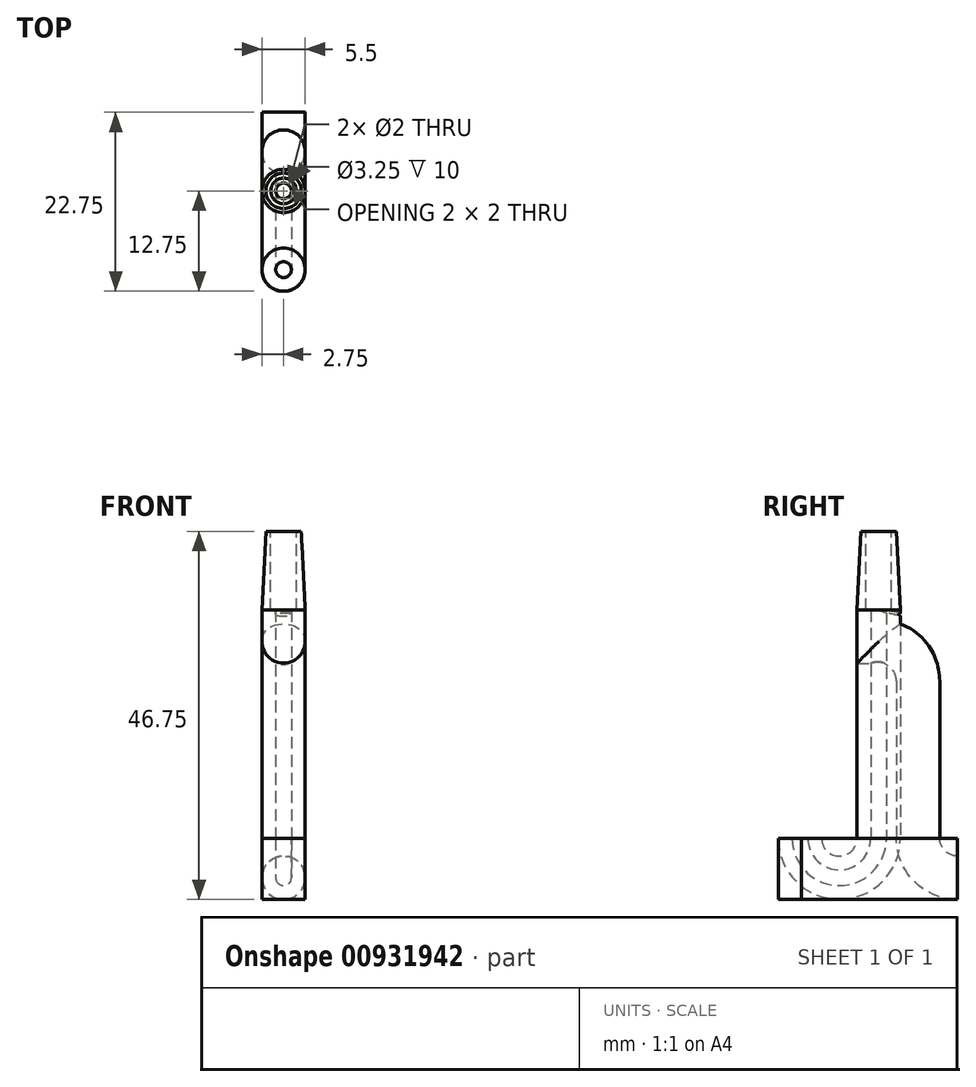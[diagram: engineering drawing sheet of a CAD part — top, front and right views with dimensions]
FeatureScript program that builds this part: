
annotation { "Feature Type Name" : "Feature", "Feature Type Description" : "" }
export const myFeature = defineFeature(function(context is Context, id is Id, definition is map)
    precondition{}
    {
        {
            var Q0;
            Q0=qCreatedBy(makeId("Front.planeOp"),FACE);
            var sketch = newSketch(context, id + "F0", { "sketchPlane" : qUnion([Q0])});
            skLineSegment(sketch, "E0", {"start": v(0, 0) * mm, "end": v(2.75, 0) * mm});
            skLineSegment(sketch, "E1", {"start": v(2.75, 0) * mm, "end": v(2.25, 10) * mm});
            skLineSegment(sketch, "E2", {"start": v(2.25, 10) * mm, "end": v(0, 10) * mm});
            skLineSegment(sketch, "E3", {"start": v(0, 10) * mm, "end": v(0, 0) * mm});
            skSolve(sketch);
        }
        {
            var Q0;
            Q0=makeQuery(id+"F0.imprint","IMPRINT",FACE,{"disambiguationData":[TD([[makeQuery(id+"F0.imprint","IMPRINT",EDGE,{"derivedFrom":sQuery(id+"F0.wireOp",EDGE,"E0")}),1.0]])]});
            var Q1;
            Q1=sQuery(id+"F0.wireOp",EDGE,"E3");
            revolve(context, id + "F1", {"surfaceOperationType" : NewSurfaceOperationType.NEW, "entities" : qUnion([Q0]), "axis" : qUnion([Q1]), "revolveType" : RevolveType.FULL});
        }
        {
            var Q0;
            Q0=makeQuery(id+"F1.opRevolve","SWEPT_FACE",FACE,{"disambiguationData":[OSD([sQuery(id+"F0.wireOp",EDGE,"E2")])]});
            var sketch = newSketch(context, id + "F2", { "sketchPlane" : qUnion([Q0])});
            skPoint(sketch, "E4", {"position": v(0, 0) * mm});
            skSolve(sketch);
        }
        {
            var Q0;
            Q0=sQuery(id+"F2.wireOp",VERTEX,"E4");
            var Q1;
            Q1=makeQuery(id+"F1.opRevolve","SWEPT_BODY",BODY,{"disambiguationData":[OSD([sQuery(id+"F0.wireOp",EDGE,"E0"),sQuery(id+"F0.wireOp",EDGE,"E1"),sQuery(id+"F0.wireOp",EDGE,"E2"),sQuery(id+"F0.wireOp",EDGE,"E3")])]});
            hole(context, id + "F3", {"style" : HoleStyle.SIMPLE, "endStyle" : HoleEndStyle.THROUGH, "holeDiameter" : 3.25 * mm, "majorDiameter" : 5 * mm, "isTappedThrough" : true, "tappedDepth" : 12 * mm, "tapClearance" : 3, "locations" : qUnion([Q0]), "scope" : qUnion([Q1])});
        }
        {
            var Q0;
            Q0=makeQuery(id+"F1.opRevolve","SWEPT_FACE",FACE,{"disambiguationData":[OSD([sQuery(id+"F0.wireOp",EDGE,"E0")])]});
            var sketch = newSketch(context, id + "F4", { "sketchPlane" : qUnion([Q0])});
            skCircle(sketch, "E5", {"center": v(0, 0) * mm, "radius": 2.75 * mm});
            skSolve(sketch);
        }
        {
            var Q0;
            Q0=qCreatedBy(makeId("Right.planeOp"),FACE);
            var sketch = newSketch(context, id + "F5", { "sketchPlane" : qUnion([Q0])});
            skPoint(sketch, "E6", {"position": v(0, -9) * mm});
            skArc(sketch, "E7", {"start": v(5, -9) * mm, "mid": v(3.54, -5.46) * mm, "end": v(0, -4) * mm});
            skPoint(sketch, "E8", {"position": v(10, -29) * mm});
            skArc(sketch, "E9", {"start": v(5, -29) * mm, "mid": v(6.46, -32.54) * mm, "end": v(10, -34) * mm});
            skLineSegment(sketch, "E10", {"start": v(5, -29) * mm, "end": v(5, -9) * mm});
            skPoint(sketch, "E11", {"position": v(-5, -29) * mm});
            skArc(sketch, "E12", {"start": v(0, -29) * mm, "mid": v(-5, -34) * mm, "end": v(-10, -29) * mm});
            skLineSegment(sketch, "E13", {"start": v(0, -4) * mm, "end": v(0, 0) * mm});
            skLineSegment(sketch, "E14", {"start": v(0, -4) * mm, "end": v(0, -9) * mm});
            skLineSegment(sketch, "E15", {"start": v(0, -9) * mm, "end": v(0, -29) * mm});
            skSolve(sketch);
        }
        {
            var Q0;
            Q0 = qSketchRegion(id + "F4", true);
            var Q1;
            Q1=sQuery(id+"F5.wireOp",EDGE,"E13");
            var Q2;
            Q2=sQuery(id+"F5.wireOp",EDGE,"E7");
            var Q3;
            Q3=sQuery(id+"F5.wireOp",EDGE,"E10");
            var Q4;
            Q4=sQuery(id+"F5.wireOp",EDGE,"E9");
            sweep(context, id + "F6", {"profiles" : qUnion([Q0]), "path" : qUnion([Q1, Q2, Q3, Q4])});
        }
        {
            var Q0;
            Q0 = qSketchRegion(id + "F4", true);
            var Q1;
            Q1=sQuery(id+"F5.wireOp",EDGE,"E13");
            var Q2;
            Q2=sQuery(id+"F5.wireOp",EDGE,"E14");
            var Q3;
            Q3=sQuery(id+"F5.wireOp",EDGE,"E15");
            var Q4;
            Q4=sQuery(id+"F5.wireOp",EDGE,"E12");
            sweep(context, id + "F7", {"profiles" : qUnion([Q0]), "path" : qUnion([Q1, Q2, Q3, Q4])});
        }
        {
            var Q0;
            Q0=qCreatedBy(makeId("Top.planeOp"),FACE);
            var sketch = newSketch(context, id + "F8", { "sketchPlane" : qUnion([Q0])});
            skCircle(sketch, "E16", {"center": v(0, 0) * mm, "radius": 1 * mm});
            skSolve(sketch);
        }
        {
            var Q0;
            Q0=qCreatedBy(makeId("Top.planeOp"),FACE);
            var sketch = newSketch(context, id + "F9", { "sketchPlane" : qUnion([Q0])});
            skArc(sketch, "E17", {"start": v(-2.75, -10) * mm, "mid": v(0.1, -12.75) * mm, "end": v(2.74, -9.81) * mm});
            skLineSegment(sketch, "E18.top", {"start": v(-2.75, 10) * mm, "end": v(2.74, 10) * mm});
            skLineSegment(sketch, "E18.left", {"start": v(-2.75, -10) * mm, "end": v(-2.75, 10) * mm});
            skLineSegment(sketch, "E18.right", {"start": v(2.74, -10) * mm, "end": v(2.74, 10) * mm});
            skSolve(sketch);
        }
        {
            var Q0;
            {var subQ0=sQuery(id+"F9.wireOp",EDGE,"E17");Q0=makeQuery(id+"F9.imprint","IMPRINT",FACE,{"disambiguationData":[TD([[makeQuery(id+"F9.imprint","IMPRINT",EDGE,{"derivedFrom":subQ0}),1.0]])]});}
            extrude(context, id + "F10", {"entities" : qUnion([Q0]), "oppositeDirection" : true, "depth" : 7.75 * mm, "offsetDistance" : 25 * mm});
        }
        {
            var Q0;
            Q0=makeQuery(id+"F10.opExtrude","SWEPT_BODY",BODY,{"disambiguationData":[OSD([sQuery(id+"F9.wireOp",EDGE,"E17"),sQuery(id+"F9.wireOp",EDGE,"E18.top"),sQuery(id+"F9.wireOp",EDGE,"E18.left"),sQuery(id+"F9.wireOp",EDGE,"E18.right")])]});
            transform(context, id + "F11", {"entities" : qUnion([Q0]), "transformType" : TransformType.TRANSLATION_3D, "dx" : 0 * mm, "dy" : 0 * mm, "dz" : -29 * mm, "makeCopy" : false});
        }
        {
            var Q0;
            Q0 = qSketchRegion(id + "F8", true);
            var Q1;
            Q1=sQuery(id+"F5.wireOp",EDGE,"E13");
            var Q2;
            Q2=sQuery(id+"F5.wireOp",EDGE,"E14");
            var Q3;
            Q3=sQuery(id+"F5.wireOp",EDGE,"E15");
            var Q4;
            Q4=sQuery(id+"F5.wireOp",EDGE,"E12");
            sweep(context, id + "F12", {"operationType" : NewBodyOperationType.REMOVE, "profiles" : qUnion([Q0]), "path" : qUnion([Q1, Q2, Q3, Q4])});
        }
        {
            var Q0;
            Q0 = qSketchRegion(id + "F8", true);
            var Q1;
            Q1=sQuery(id+"F5.wireOp",EDGE,"cYiUkW4Y-SU42-EtDn-rcv1-GgWZnFMX7ThN");
            var Q2;
            Q2=sQuery(id+"F5.wireOp",EDGE,"E12");
            sweep(context, id + "F13", {"operationType" : NewBodyOperationType.REMOVE, "profiles" : qUnion([Q0]), "path" : qUnion([Q1, Q2])});
        }
    });
